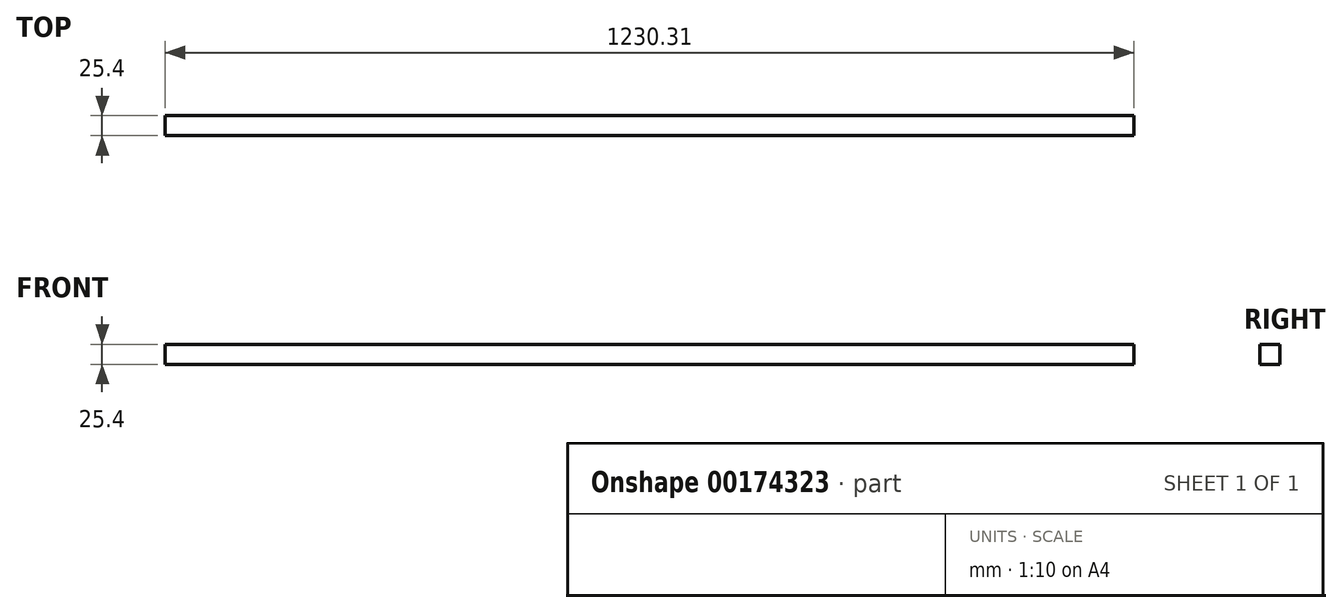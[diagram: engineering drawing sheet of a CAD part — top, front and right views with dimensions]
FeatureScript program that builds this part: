
annotation { "Feature Type Name" : "Feature", "Feature Type Description" : "" }
export const myFeature = defineFeature(function(context is Context, id is Id, definition is map)
    precondition{}
    {
        {
            var Q0;
            Q0=qCreatedBy(makeId("Front.planeOp"),FACE);
            var sketch = newSketch(context, id + "F0", { "sketchPlane" : qUnion([Q0])});
            skLineSegment(sketch, "E0.bottom", {"start": v(0, 0) * mm, "end": v(1230.31, 0) * mm});
            skLineSegment(sketch, "E0.top", {"start": v(0, 25.4) * mm, "end": v(1230.31, 25.4) * mm});
            skLineSegment(sketch, "E0.left", {"start": v(0, 0) * mm, "end": v(0, 25.4) * mm});
            skLineSegment(sketch, "E0.right", {"start": v(1230.31, 0) * mm, "end": v(1230.31, 25.4) * mm});
            skSolve(sketch);
        }
        {
            var Q0;
            Q0=makeQuery(id+"F0.imprint","IMPRINT",FACE,{"disambiguationData":[TD([[makeQuery(id+"F0.imprint","IMPRINT",EDGE,{"derivedFrom":sQuery(id+"F0.wireOp",EDGE,"E0.bottom")}),1.0]])]});
            extrude(context, id + "F1", {"entities" : qUnion([Q0]), "depth" : 25.4 * mm});
        }
    });
